# Revit family: НЕВАТОМ_Neiva 2 подвесная CX-Е-R 600, Версия 2
name_source: partatom
category: Оборудование
revit_build: Autodesk Revit 2017 (Build: 20170118_1100(x64)
units: mm (PartAtom-declared; Revit-internal decimal feet)

## family parameters
Всегда вертикально = Нет
На основе рабочей плоскости = Да
Общий = Нет
При загрузке вырезать с полостями = Нет
Размер круглого соединителя = Использовать диаметр
Тип детали = Нормальный
Точка расчета площади = Нет

## types (1)
- СX-600-E-R
    A1 = 500 мм
    A6 = 270 мм
    ADSK_Единица измерения = шт.
    ADSK_Завод-изготовитель = НЕВАТОМ
    ADSK_Количество = 1
    ADSK_Количество фаз = 3
    ADSK_Количество фаз числовое = 3
    ADSK_Коэффициент мощности = 0.8
    ADSK_Марка = СX-600-E-R
    ADSK_Масса = 109
    ADSK_Наименование = СX-600-E-R
    ADSK_Напряжение = 220 В
    ADSK_Номинальная мощность = 168 Вт
    ADSK_Полная мощность = 210 В·А
    ADSK_Потеря давления воздуха = 0.0 Па
    ADSK_Размер_Высота = 362 мм
    ADSK_Размер_Длина = 1460 мм
    ADSK_Размер_Ширина = 1122 мм
    ADSK_Расход воздуха = 0.0 м³/ч
    ADSK_Расход жидкости = 0.0 м³/ч
    ADSK_Ток = 1 А
    ADSK_материал = материал курпуса
    B = 1122 мм
    H1 = 362 мм
    L = 1460 мм
    Nevatom_URL = https://t.me
    Nevatom_Для задания электроснабжения = 380 В
    Nevatom_Мощность нагревателя = 4500 Вт
    Nevatom_Напорная характеристика, P = 0.0 Па
    Nevatom_Напорная характеристика, Р1 = 350.0 Па
    Nevatom_Производительность = 300-900 м³/ч
    b двигателя = 537 мм
    b1 = 123 мм
    d штуцер = 0 мм
    h = 0 мм
    h двигателя = 362 мм
    h3 = 280 мм
    h4 = 62 мм
    k = 20 мм
    l = 271 мм
    l двигателя = 1 мм
    l штуцер = 125 мм
    l1 = 757 мм
    m = 271 мм
    Отметка по умолчанию = 1219 мм
    а = 456 мм
    а1 = 40 мм
